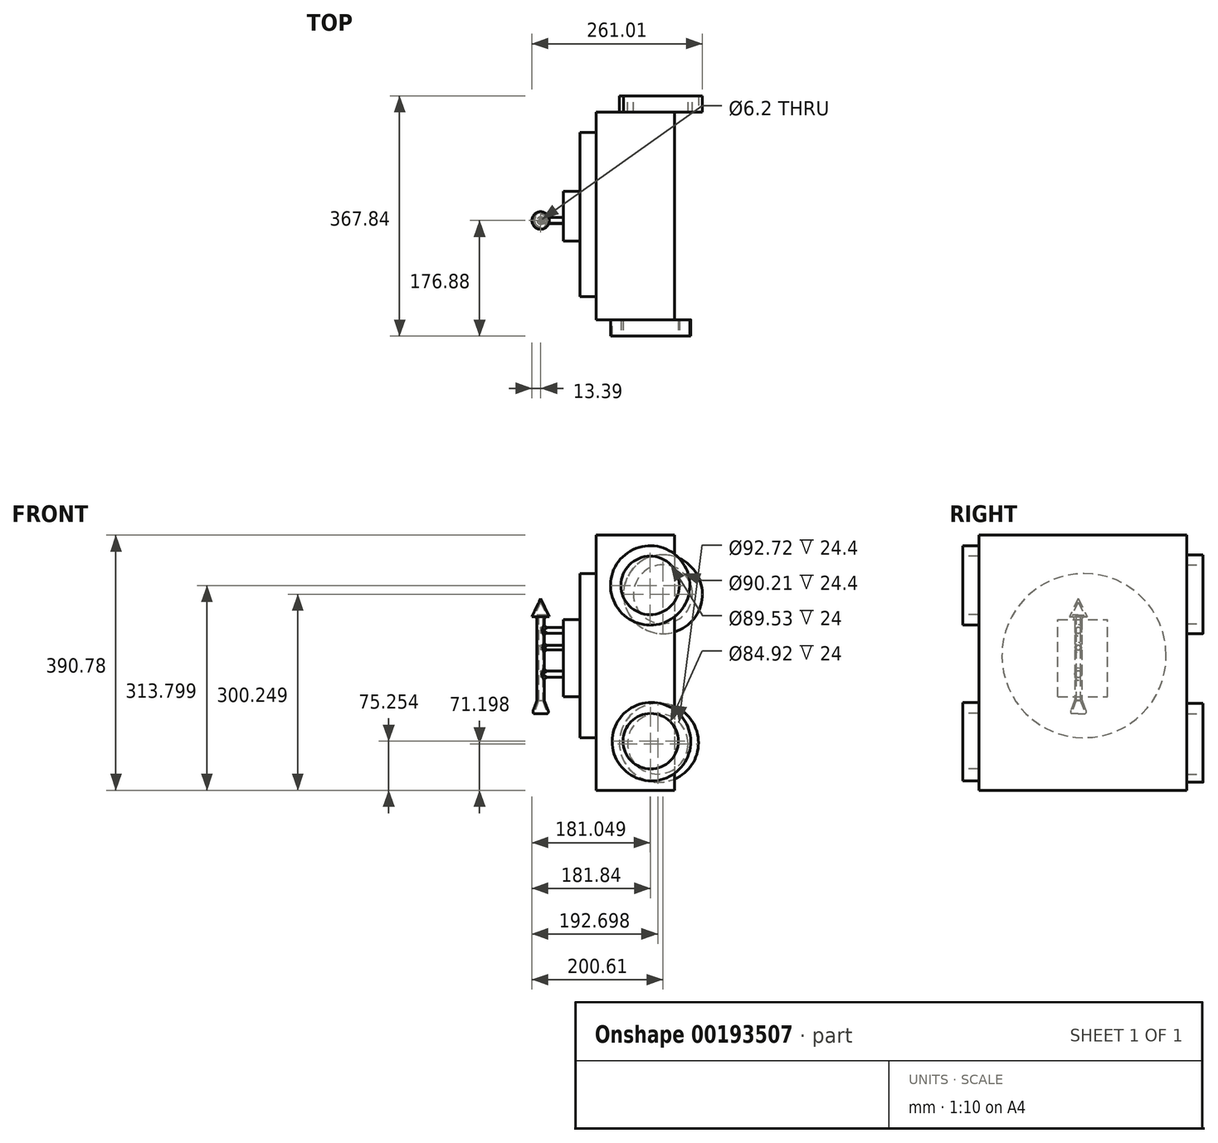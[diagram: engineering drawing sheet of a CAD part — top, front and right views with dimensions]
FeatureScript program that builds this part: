
annotation { "Feature Type Name" : "Feature", "Feature Type Description" : "" }
export const myFeature = defineFeature(function(context is Context, id is Id, definition is map)
    precondition{}
    {
        {
            var Q0;
            Q0=qCreatedBy(makeId("Front.planeOp"),FACE);
            var sketch = newSketch(context, id + "F0", { "sketchPlane" : qUnion([Q0])});
            skLineSegment(sketch, "E0", {"start": v(0, 102.27) * mm, "end": v(13.4, 74.51) * mm});
            skLineSegment(sketch, "E1", {"start": v(13.4, 74.51) * mm, "end": v(5.6, 74.51) * mm});
            skLineSegment(sketch, "E2", {"start": v(5.6, 74.51) * mm, "end": v(5.6, -53.57) * mm});
            skLineSegment(sketch, "E3", {"start": v(5.6, -53.57) * mm, "end": v(13.4, -74.03) * mm});
            skLineSegment(sketch, "E4", {"start": v(13.4, -74.03) * mm, "end": v(0, -74.03) * mm});
            skLineSegment(sketch, "E5", {"start": v(0, -74.03) * mm, "end": v(0, 102.27) * mm});
            skSolve(sketch);
        }
        {
            var Q0;
            Q0 = qSketchRegion(id + "F0", true);
            var Q1;
            Q1=sQuery(id+"F0.wireOp",EDGE,"E5");
            revolve(context, id + "F1", {"entities" : qUnion([Q0]), "axis" : qUnion([Q1]), "revolveType" : RevolveType.FULL});
        }
        {
            var Q0;
            Q0=makeQuery(id+"F1.opRevolve","SWEPT_FACE",FACE,{"disambiguationData":[OSD([sQuery(id+"F0.wireOp",EDGE,"E4")])]});
            shell(context, id + "F2", {"entities" : qUnion([Q0]), "thickness" : 2.5 * mm});
        }
        {
            var Q0;
            Q0=qCreatedBy(makeId("Right.planeOp"),FACE);
            var sketch = newSketch(context, id + "F3", { "sketchPlane" : qUnion([Q0])});
            skCircle(sketch, "E6", {"center": v(0, 53.57) * mm, "radius": 4.39 * mm});
            skCircle(sketch, "E7", {"center": v(0, -13.64) * mm, "radius": 4.88 * mm});
            skCircle(sketch, "E8", {"center": v(0, 27.02) * mm, "radius": 3.53 * mm});
            skSolve(sketch);
        }
        {
            var Q0;
            Q0=sQuery(id+"F3.wireOp",EDGE,"E6");
            extrude(context, id + "F4", {"bodyType" : ToolBodyType.SURFACE, "surfaceEntities" : qUnion([Q0]), "depth" : 34 * mm});
        }
        {
            var Q0;
            Q0 = qSketchRegion(id + "F3", true);
            extrude(context, id + "F5", {"entities" : qUnion([Q0]), "operationType" : NewBodyOperationType.ADD, "depth" : 35 * mm});
        }
        {
            var Q0;
            Q0=makeQuery(id+"F1.opRevolve","SWEPT_FACE",FACE,{"disambiguationData":[OSD([sQuery(id+"F0.wireOp",EDGE,"E3")])]});
            var Q1;
            Q1=makeQuery(id+"F1.opRevolve","SWEPT_FACE",FACE,{"disambiguationData":[OSD([sQuery(id+"F0.wireOp",EDGE,"E2")])]});
            fillet(context, id + "F6", {"entities" : qUnion([Q0, Q1]), "radius" : 5 * mm, "tangentPropagation" : true, "allowEdgeOverflow" : false});
        }
        {
            var Q0;
            Q0=makeQuery(id+"F5.opExtrude","CAP_FACE",FACE,{"disambiguationData":[OSD([sQuery(id+"F3.wireOp",EDGE,"E7")])],"isStart":false});
            var sketch = newSketch(context, id + "F7", { "sketchPlane" : qUnion([Q0])});
            skLineSegment(sketch, "E9.bottom", {"start": v(-31.22, -48.42) * mm, "end": v(44.62, -48.42) * mm});
            skLineSegment(sketch, "E9.top", {"start": v(-31.22, 70.17) * mm, "end": v(44.62, 70.17) * mm});
            skLineSegment(sketch, "E9.left", {"start": v(-31.22, -48.42) * mm, "end": v(-31.22, 70.17) * mm});
            skLineSegment(sketch, "E9.right", {"start": v(44.62, -48.42) * mm, "end": v(44.62, 70.17) * mm});
            skSolve(sketch);
        }
        {
            var Q0;
            Q0 = qSketchRegion(id + "F7", true);
            extrude(context, id + "F8", {"entities" : qUnion([Q0]), "operationType" : NewBodyOperationType.ADD, "depth" : 25 * mm});
        }
        {
            var Q0;
            Q0=makeQuery(id+"F8.opExtrude","CAP_FACE",FACE,{"disambiguationData":[OSD([sQuery(id+"F7.wireOp",EDGE,"E9.bottom"),sQuery(id+"F7.wireOp",EDGE,"E9.top"),sQuery(id+"F7.wireOp",EDGE,"E9.left"),sQuery(id+"F7.wireOp",EDGE,"E9.right")])],"isStart":false});
            var sketch = newSketch(context, id + "F9", { "sketchPlane" : qUnion([Q0])});
            skCircle(sketch, "E10", {"center": v(8.93, 14.76) * mm, "radius": 125.73 * mm});
            skSolve(sketch);
        }
        {
            var Q0;
            Q0 = qSketchRegion(id + "F9", true);
            extrude(context, id + "F10", {"entities" : qUnion([Q0]), "operationType" : NewBodyOperationType.ADD, "depth" : 25 * mm});
        }
        {
            var Q0;
            Q0=makeQuery(id+"F10.opExtrude","CAP_FACE",FACE,{"disambiguationData":[OSD([sQuery(id+"F9.wireOp",EDGE,"E10")])],"isStart":false});
            var sketch = newSketch(context, id + "F11", { "sketchPlane" : qUnion([Q0])});
            skLineSegment(sketch, "E11.bottom", {"start": v(165.96, 199.3) * mm, "end": v(-151.88, 199.3) * mm});
            skLineSegment(sketch, "E11.top", {"start": v(165.96, -191.47) * mm, "end": v(-151.88, -191.47) * mm});
            skLineSegment(sketch, "E11.left", {"start": v(165.96, 199.3) * mm, "end": v(165.96, -191.47) * mm});
            skLineSegment(sketch, "E11.right", {"start": v(-151.88, 199.3) * mm, "end": v(-151.88, -191.47) * mm});
            skSolve(sketch);
        }
        {
            var Q0;
            Q0 = qSketchRegion(id + "F11", true);
            extrude(context, id + "F12", {"entities" : qUnion([Q0]), "operationType" : NewBodyOperationType.ADD, "depth" : 120 * mm});
        }
        {
            var Q0;
            Q0=makeQuery(id+"F12.opExtrude","SWEPT_FACE",FACE,{"disambiguationData":[OSD([sQuery(id+"F11.wireOp",EDGE,"E11.left")])]});
            var sketch = newSketch(context, id + "F13", { "sketchPlane" : qUnion([Q0])});
            skCircle(sketch, "E12", {"center": v(-187.22, 108.78) * mm, "radius": 60.4 * mm});
            skCircle(sketch, "E13", {"center": v(-181.05, -118.7) * mm, "radius": 60.55 * mm});
            skSolve(sketch);
        }
        {
            var Q0;
            Q0 = qSketchRegion(id + "F13", true);
            extrude(context, id + "F14", {"entities" : qUnion([Q0]), "operationType" : NewBodyOperationType.ADD, "depth" : 25 * mm});
        }
        {
            var Q0;
            Q0=makeQuery(id+"F12.opExtrude","SWEPT_FACE",FACE,{"disambiguationData":[OSD([sQuery(id+"F11.wireOp",EDGE,"E11.right")])]});
            var sketch = newSketch(context, id + "F15", { "sketchPlane" : qUnion([Q0])});
            skCircle(sketch, "E14", {"center": v(169.66, -116.9) * mm, "radius": 60.13 * mm});
            skCircle(sketch, "E15", {"center": v(167.66, 122.33) * mm, "radius": 60.75 * mm});
            skSolve(sketch);
        }
        {
            var Q0;
            Q0 = qSketchRegion(id + "F15", true);
            extrude(context, id + "F16", {"entities" : qUnion([Q0]), "operationType" : NewBodyOperationType.ADD, "depth" : 25 * mm});
        }
        {
            var Q0;
            Q0=makeQuery(id+"F14.opExtrude","CAP_FACE",FACE,{"disambiguationData":[OSD([sQuery(id+"F13.wireOp",EDGE,"E12")])],"isStart":false});
            var sketch = newSketch(context, id + "F17", { "sketchPlane" : qUnion([Q0])});
            skCircle(sketch, "E16", {"center": v(-187.22, 108.78) * mm, "radius": 45.1 * mm});
            skCircle(sketch, "E17", {"center": v(-179.3, -120.27) * mm, "radius": 46.36 * mm});
            skSolve(sketch);
        }
        {
            var Q0;
            Q0 = qSketchRegion(id + "F17", true);
            extrude(context, id + "F18", {"entities" : qUnion([Q0]), "operationType" : NewBodyOperationType.REMOVE, "oppositeDirection" : true, "depth" : 24.4 * mm});
        }
        {
            var Q0;
            Q0=makeQuery(id+"F16.opExtrude","CAP_FACE",FACE,{"disambiguationData":[OSD([sQuery(id+"F15.wireOp",EDGE,"E15")])],"isStart":false});
            var sketch = newSketch(context, id + "F19", { "sketchPlane" : qUnion([Q0])});
            skCircle(sketch, "E18", {"center": v(168.45, -116.22) * mm, "radius": 42.46 * mm});
            skCircle(sketch, "E19", {"center": v(167.66, 122.33) * mm, "radius": 44.77 * mm});
            skSolve(sketch);
        }
        {
            var Q0;
            Q0 = qSketchRegion(id + "F19", true);
            extrude(context, id + "F20", {"entities" : qUnion([Q0]), "operationType" : NewBodyOperationType.REMOVE, "oppositeDirection" : true, "depth" : 24 * mm});
        }
    });
